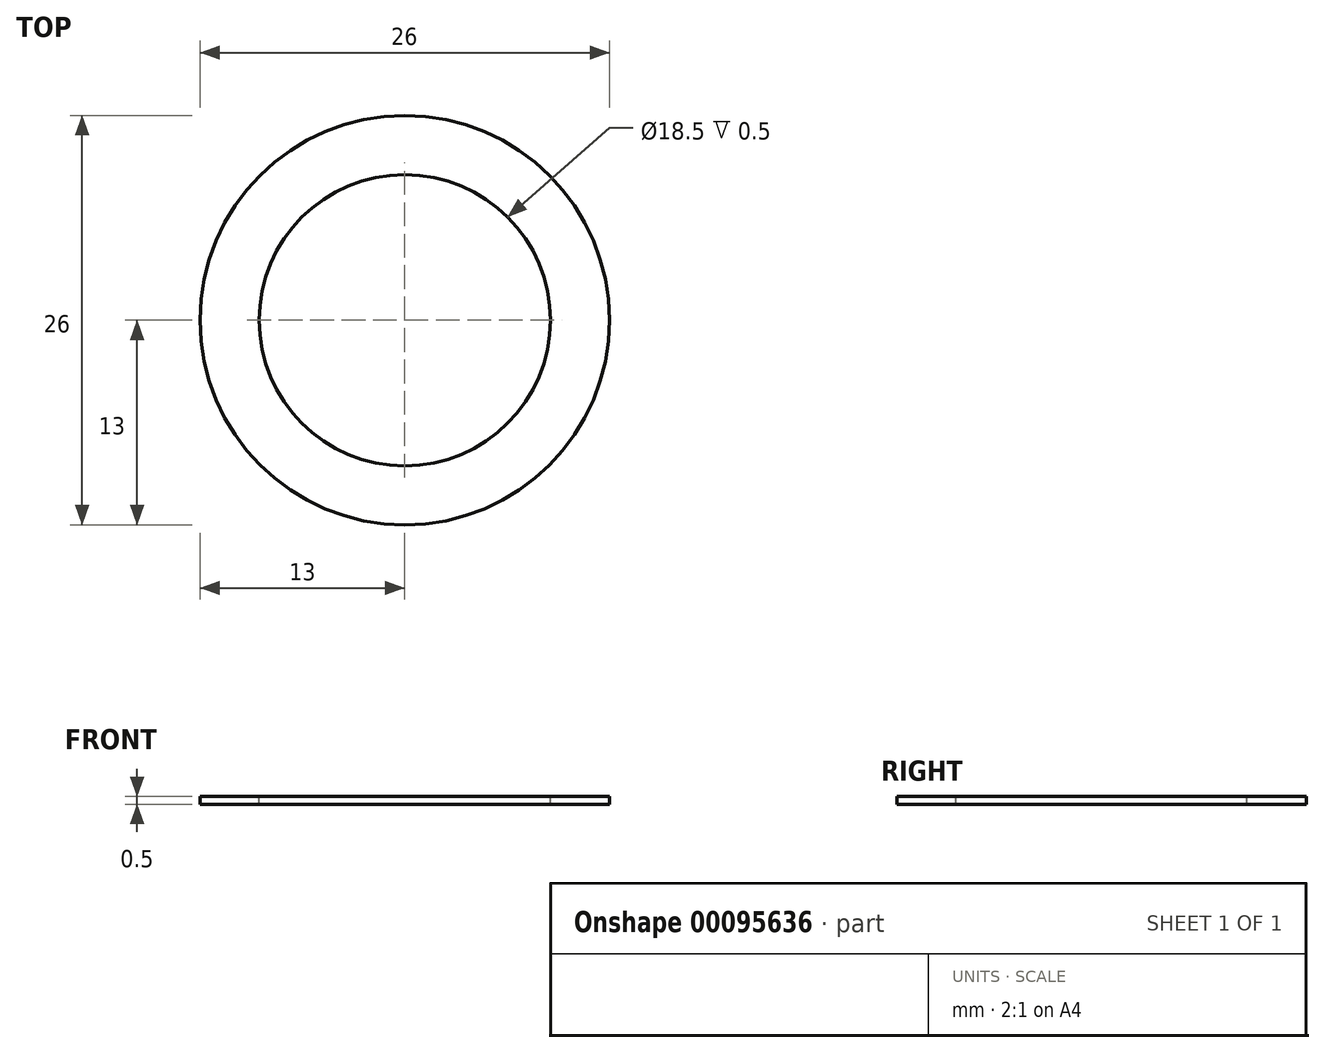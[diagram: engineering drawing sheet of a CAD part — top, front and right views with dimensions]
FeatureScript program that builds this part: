
annotation { "Feature Type Name" : "Feature", "Feature Type Description" : "" }
export const myFeature = defineFeature(function(context is Context, id is Id, definition is map)
    precondition{}
    {
        {
            var Q0;
            Q0=qCreatedBy(makeId("Top.planeOp"),FACE);
            var sketch = newSketch(context, id + "F0", { "sketchPlane" : qUnion([Q0])});
            skCircle(sketch, "E0", {"center": v(0, 0) * mm, "radius": 13 * mm});
            skSolve(sketch);
        }
        {
            var Q0;
            Q0=qSketchRegion(id+"F0",true);
            extrude(context, id + "F1", {"entities" : qUnion([Q0]), "depth" : .5 * mm});
        }
        {
            var Q0;
            Q0=makeQuery(id+"F1.opExtrude","CAP_FACE",FACE,{"disambiguationData":[OSD([sQuery(id+"F0.wireOp",EDGE,"E0")])],"isStart":false});
            var sketch = newSketch(context, id + "F2", { "sketchPlane" : qUnion([Q0])});
            skCircle(sketch, "E1", {"center": v(0, 0) * mm, "radius": 9.25 * mm});
            skSolve(sketch);
        }
        {
            var Q0;
            Q0=qSketchRegion(id+"F2",true);
            extrude(context, id + "F3", {"entities" : qUnion([Q0]), "operationType" : NewBodyOperationType.REMOVE, "oppositeDirection" : true, "depth" : 25 * mm});
        }
    });
